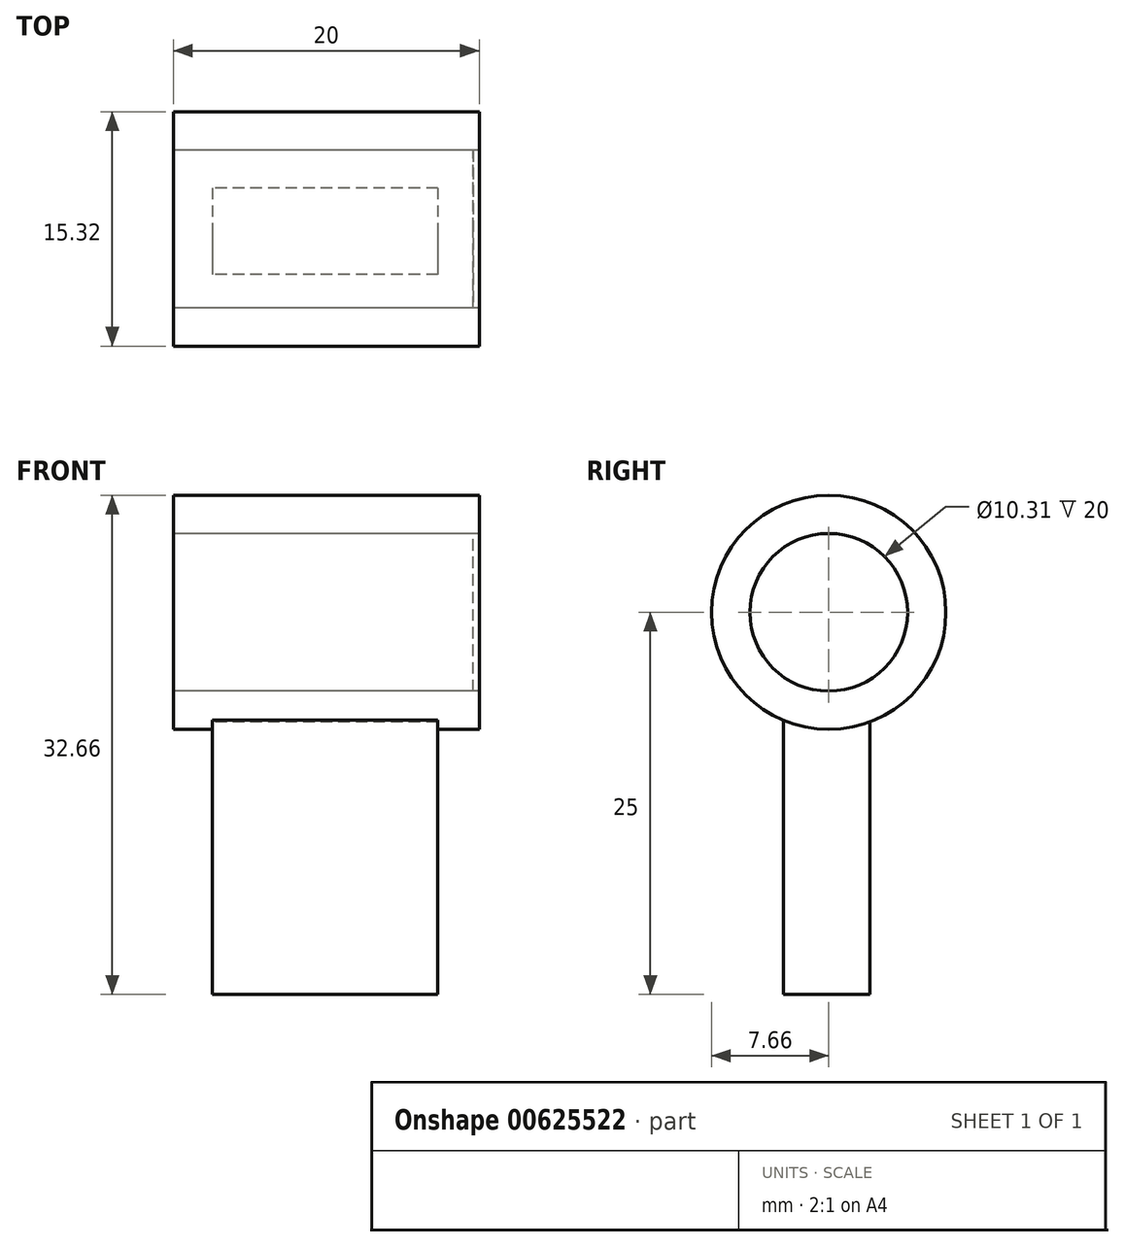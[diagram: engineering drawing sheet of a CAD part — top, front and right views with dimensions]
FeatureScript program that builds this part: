
annotation { "Feature Type Name" : "Feature", "Feature Type Description" : "" }
export const myFeature = defineFeature(function(context is Context, id is Id, definition is map)
    precondition{}
    {
        {
            var Q0;
            Q0=qCreatedBy(makeId("Right.planeOp"),FACE);
            var sketch = newSketch(context, id + "F0", { "sketchPlane" : qUnion([Q0])});
            skCircle(sketch, "E0", {"center": v(0, 0) * mm, "radius": 7.66 * mm});
            skSolve(sketch);
        }
        {
            var Q0;
            Q0 = qSketchRegion(id + "F0", true);
            extrude(context, id + "F1", {"entities" : qUnion([Q0]), "depth" : 20 * mm, "offsetDistance" : 25 * mm});
        }
        {
            var Q0;
            Q0=qCreatedBy(makeId("Top.planeOp"),FACE);
            var sketch = newSketch(context, id + "F2", { "sketchPlane" : qUnion([Q0])});
            skLineSegment(sketch, "E1.bottom", {"start": v(2.55, 2.7) * mm, "end": v(17.28, 2.7) * mm});
            skLineSegment(sketch, "E1.top", {"start": v(2.55, -2.97) * mm, "end": v(17.28, -2.97) * mm});
            skLineSegment(sketch, "E1.left", {"start": v(2.55, 2.7) * mm, "end": v(2.55, -2.97) * mm});
            skLineSegment(sketch, "E1.right", {"start": v(17.28, 2.7) * mm, "end": v(17.28, -2.97) * mm});
            skSolve(sketch);
        }
        {
            var Q0;
            Q0 = qSketchRegion(id + "F2", true);
            extrude(context, id + "F3", {"entities" : qUnion([Q0]), "operationType" : NewBodyOperationType.ADD, "oppositeDirection" : true, "depth" : 25 * mm, "offsetDistance" : 25 * mm});
        }
        {
            var Q0;
            Q0=qCreatedBy(makeId("Right.planeOp"),FACE);
            var sketch = newSketch(context, id + "F4", { "sketchPlane" : qUnion([Q0])});
            skCircle(sketch, "E2", {"center": v(0, 0) * mm, "radius": 5.16 * mm});
            skSolve(sketch);
        }
        {
            var Q0;
            Q0 = qSketchRegion(id + "F4", true);
            extrude(context, id + "F5", {"entities" : qUnion([Q0]), "operationType" : NewBodyOperationType.REMOVE, "depth" : 38.2 * mm, "offsetDistance" : 25 * mm});
        }
        {
            var Q0;
            Q0 = qSketchRegion(id + "F4", true);
            extrude(context, id + "F6", {"entities" : qUnion([Q0]), "depth" : 19.6 * mm, "offsetDistance" : 25 * mm});
        }
    });
